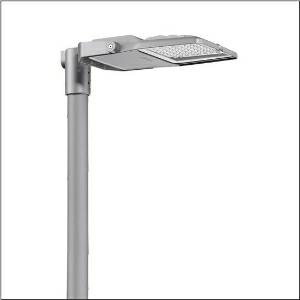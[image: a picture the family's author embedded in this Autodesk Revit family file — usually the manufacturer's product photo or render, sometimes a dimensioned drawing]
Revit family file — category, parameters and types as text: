
# Revit family: floodlight_fl_21_mini___pl52_5xa7772b2d3a_4e36
name_source: partatom
category: Lighting Fixtures
units: mm (PartAtom-declared; Revit-internal decimal feet)

## family parameters
Cut with Voids When Loaded = No
Host = Face
Light Source = No
Part Type = Normal
Room Calculation Point = No
Round Connector Dimension = Use Diameter
Shared = No

## types (1)
- --- (1 x LED, 6240 lm, 45.5 W, 3000K)
    Apparent Load = 46 VA
    CIE Flux Codes = 26 60 98 100 100
    Color Rendering = 70
    Color Temperature = 3000K
    Default Elevation = 1800 mm
    Description = Floodlight FL 21 mini, floodlight, primary light control with lens, of PMMA, primary optical cover: protective disc, of toughened safety glass, transparent, light distribution: PL52, light emission: direct distribution, installation type: surface-mounted, LED, High Power LED, rated luminous flux: 6.240lm, luminous efficacy: 137lm/W, light colour: 730, colour temperature: 3000K, control gear: ECG iQ, control: Auto-Match, Temp-Guard, Night-Set, Smart-Wire, Desk-Remote (wireless, voltage-free reading and setting of iQ features in the workshop via application-optimized NFC function/RFID function), optimised constant luminous flux control (CLO 2.0), Light-Fading, Lumen-Switch, with terminal, 6-pole, mains connection: 220..240V, AC, 50/60Hz, start of lifetime: 46W, end of lifetime: 48W, reduction: 22W, luminaire housing, of diecast aluminium, powder-coated, Siteco® metallic grey (DB 702S), corrosivity category C5 according to DIN EN ISO 12944, mast bracket, of steel, galvanised, powder-coated, protection rating (complete): IP66, insulation class (complete): insulation class II (safety insulation), certification: CE, ENEC, VDE, protection symbol: D, impact resistance: IK08, permissible operating ambient temperature: -40..+40°C, permissible operating ambient temperature for outdoor applications: -40..+50°C, standard: DIN EN 12944, packaging unit: 1 piece

Light Distribution: PL52
    Height = 70 mm
    Lamp = 1 x LED
    Lamp Light Flux = 6240 lm
    Lamp Power = 45.5 W
    Lamp count = 1
    Length = 485 mm
    Luminous efficacy = 137 lm/W
    Manufacturer = Siteco
    ModVariant = No
    Model = 5XA7772B2D3A
    Number of Poles = 1
    OnlyDefault = Yes
    Power Factor = 1
    Product Name = Floodlight FL 21 mini | PL52
    Product group = floodlight | pylon top
    ProductGroupID = 6101
    Protection Class = Protection class II
    Protection Degree = IP 66
    RLX_Detail_Level = 1
    RlxData = <blob elided: 101373 chars, md5=a52b29ef>
    Socket = socket
    Standby Power = 0 W
    System Light Flux = 6240 lm
    System Power = 46 W
    Type Comments = factory setting: luminous flux: 100 % | dim-lin: 254 | 463 mA
    Type Image = l_1007125.jpg
    URL = http://relux.com
    VarID = @adj_075963
    Voltage = 0 V
    Weight = 0.00 kg
    Width = 337 mm

## geometry (parser evidence)
native form markers: Blend x4, Sweep x14
no freeform markers — native parametric forms only
